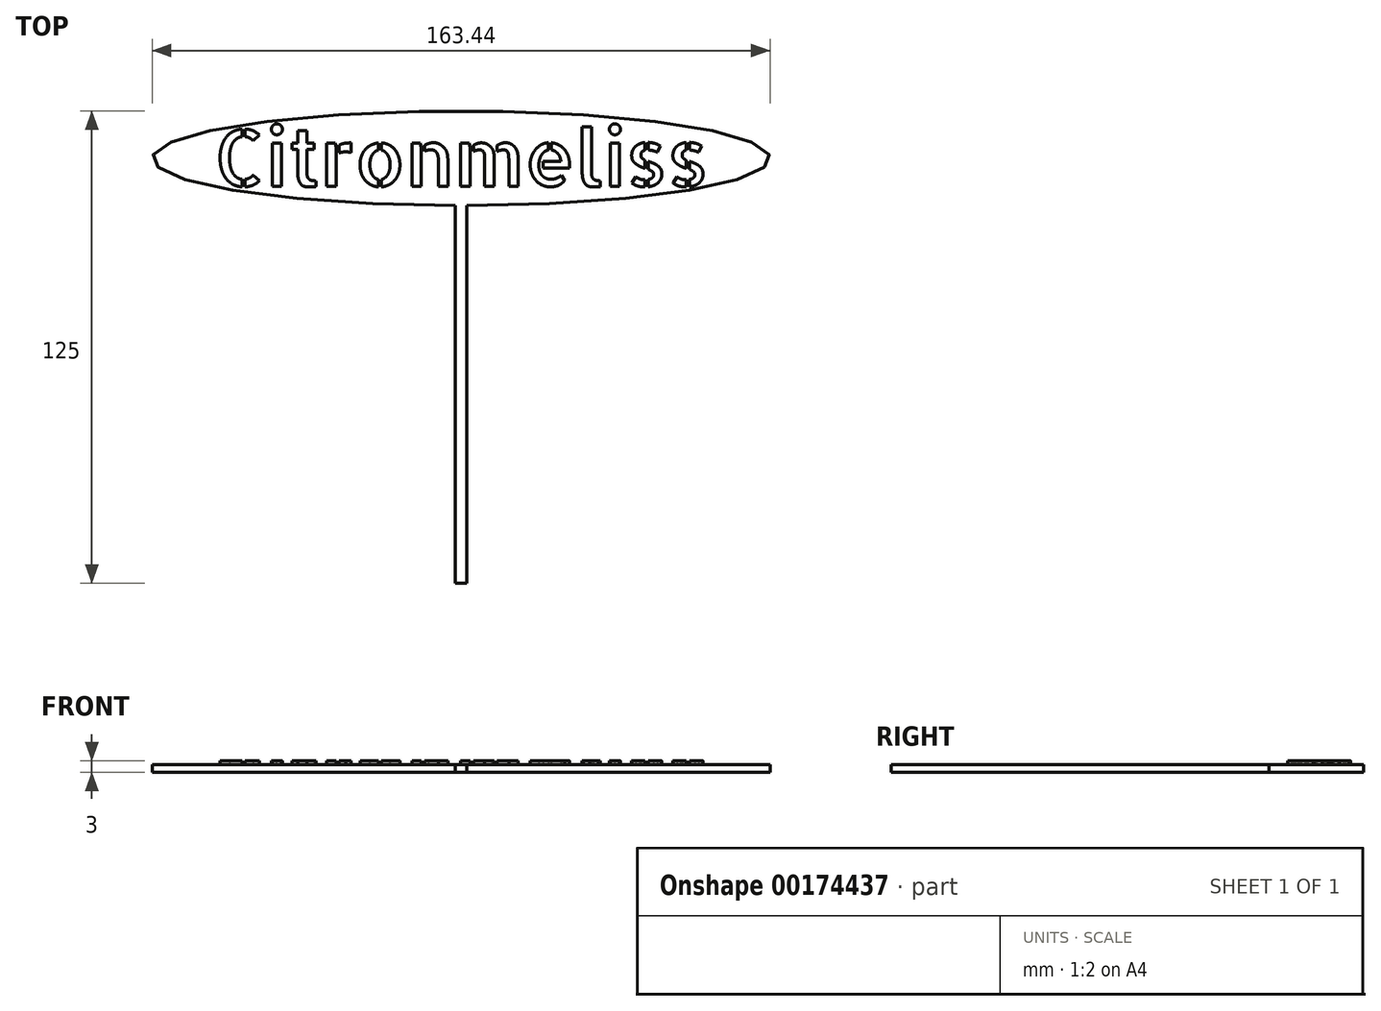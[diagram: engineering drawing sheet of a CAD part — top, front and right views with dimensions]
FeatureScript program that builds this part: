
annotation { "Feature Type Name" : "Feature", "Feature Type Description" : "" }
export const myFeature = defineFeature(function(context is Context, id is Id, definition is map)
    precondition{}
    {
        {
            var Q0;
            Q0=qCreatedBy(makeId("Top.planeOp"),FACE);
            var sketch = newSketch(context, id + "F0", { "sketchPlane" : qUnion([Q0])});
            skText(sketch, "E0", { "text": "Citronmeliss", "fontName": "AllertaStencil-Regular.ttf"});
            const initialGuessF0  = {"E0": [-0.06538, -0.0075, 1, 0, 0.015]};
            skSetInitialGuess(sketch, initialGuessF0);
            skSolve(sketch);
        }
        {
            var Q0;
            Q0=qCreatedBy(makeId("Top.planeOp"),FACE);
            var sketch = newSketch(context, id + "F1", { "sketchPlane" : qUnion([Q0])});
            skEllipticalArc(sketch, "E1", {});
            skLineSegment(sketch, "E2.top", {"start": v(-1.5, -112.5) * mm, "end": v(1.5, -112.5) * mm});
            skLineSegment(sketch, "E2.left", {"start": v(-1.5, -12.5) * mm, "end": v(-1.5, -112.5) * mm});
            skLineSegment(sketch, "E2.right", {"start": v(1.5, -12.5) * mm, "end": v(1.5, -112.5) * mm});
            const initialGuessF1  = {"E1": [0, 0, 1, 0, 0.08172200520833482, 0.0125, 4.7307449205579895, 4.69403304021139]};
            skSetInitialGuess(sketch, initialGuessF1);
            skSolve(sketch);
        }
        {
            var Q0;
            Q0 = qSketchRegion(id + "F1", true);
            extrude(context, id + "F2", {"entities" : qUnion([Q0]), "depth" : 2 * mm});
        }
        {
            var Q0;
            Q0 = qSketchRegion(id + "F0", true);
            extrude(context, id + "F3", {"entities" : qUnion([Q0]), "operationType" : NewBodyOperationType.ADD, "depth" : 3 * mm});
        }
    });
